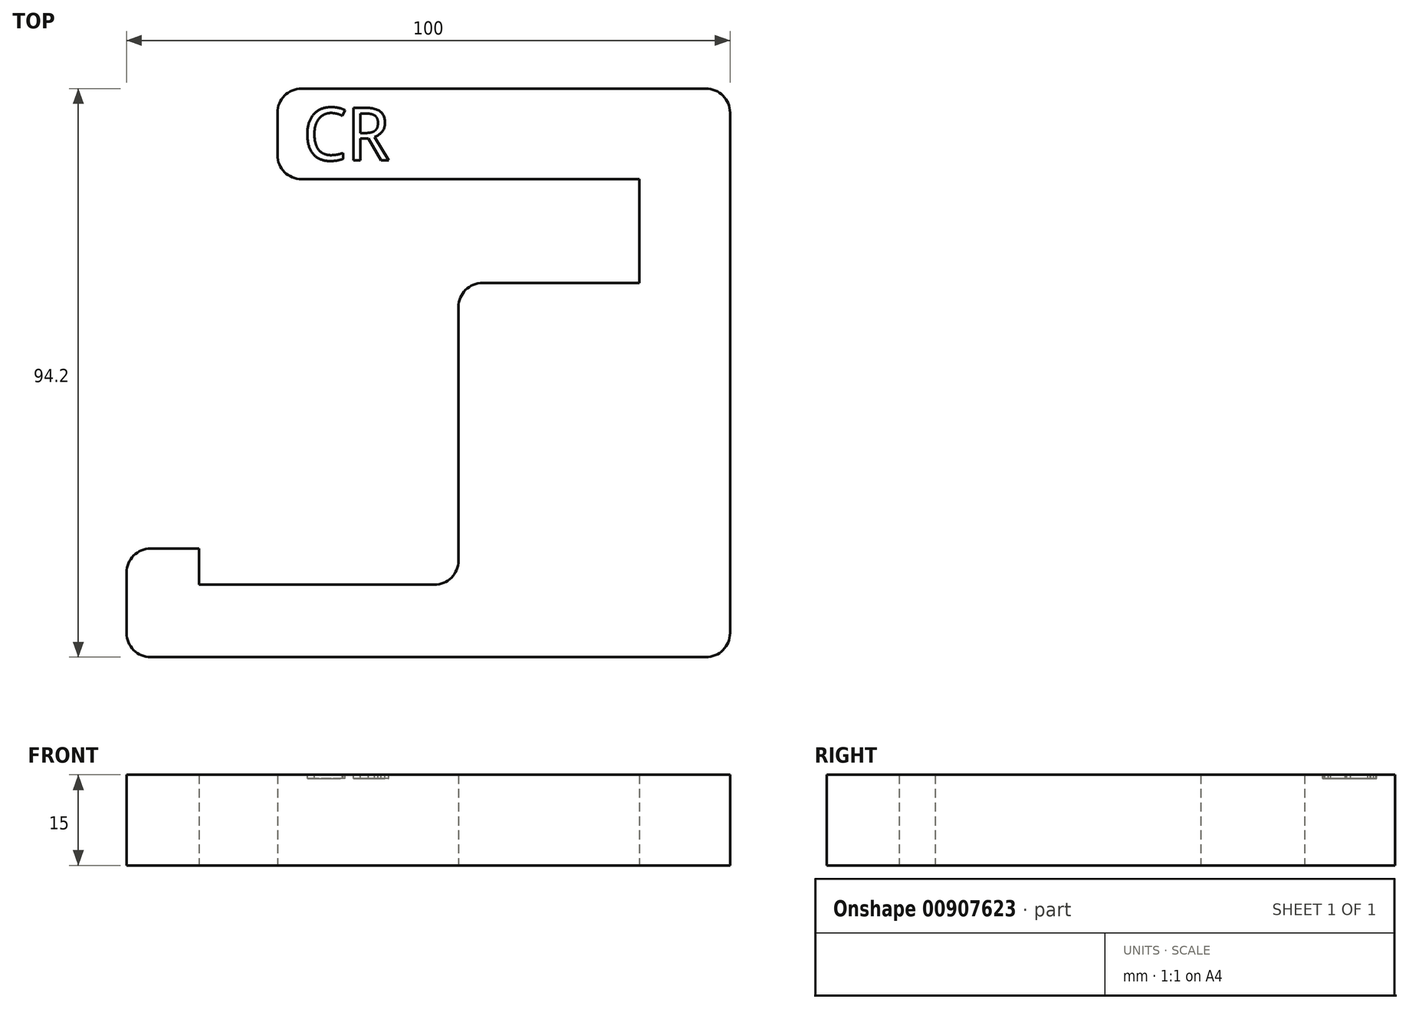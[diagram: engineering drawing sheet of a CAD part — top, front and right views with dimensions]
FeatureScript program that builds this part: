
annotation { "Feature Type Name" : "Feature", "Feature Type Description" : "" }
export const myFeature = defineFeature(function(context is Context, id is Id, definition is map)
    precondition{}
    {
        {
            var Q0;
            Q0=qCreatedBy(makeId("Top.planeOp"),FACE);
            var sketch = newSketch(context, id + "F0", { "sketchPlane" : qUnion([Q0])});
            skLineSegment(sketch, "E0", {"start": v(0, 0) * mm, "end": v(0, -15) * mm});
            skLineSegment(sketch, "E1", {"start": v(0, -15) * mm, "end": v(60, -15) * mm});
            skLineSegment(sketch, "E2", {"start": v(60, -15) * mm, "end": v(60, -32.2) * mm});
            skLineSegment(sketch, "E3", {"start": v(60, -32.2) * mm, "end": v(30, -32.2) * mm});
            skLineSegment(sketch, "E4", {"start": v(30, -32.2) * mm, "end": v(30, -82.2) * mm});
            skLineSegment(sketch, "E5", {"start": v(-25, -94.2) * mm, "end": v(75, -94.2) * mm});
            skLineSegment(sketch, "E6", {"start": v(75, -94.2) * mm, "end": v(75, 0) * mm});
            skLineSegment(sketch, "E7", {"start": v(75, 0) * mm, "end": v(0, 0) * mm});
            skLineSegment(sketch, "E8", {"start": v(-25, -76.2) * mm, "end": v(-13, -76.2) * mm});
            skLineSegment(sketch, "E9", {"start": v(-13, -76.2) * mm, "end": v(-13, -82.2) * mm});
            skLineSegment(sketch, "E10", {"start": v(-13, -82.2) * mm, "end": v(30, -82.2) * mm});
            skLineSegment(sketch, "E11", {"start": v(-25, -76.2) * mm, "end": v(-25, -94.2) * mm});
            skSolve(sketch);
        }
        {
            var Q0;
            Q0=qSketchRegion(id+"F0",true);
            extrude(context, id + "F1", {"entities" : qUnion([Q0]), "depth" : 15 * mm, "offsetDistance" : 25 * mm});
        }
        {
            var Q0;
            Q0=makeQuery(id+"F1.opExtrude","SWEPT_EDGE",EDGE,{"disambiguationData":[OSD([sQuery(id+"F0.wireOp",EDGE,"E3"),sQuery(id+"F0.wireOp",EDGE,"E4")])]});
            var Q1;
            Q1=makeQuery(id+"F1.opExtrude","SWEPT_EDGE",EDGE,{"disambiguationData":[OSD([sQuery(id+"F0.wireOp",EDGE,"E0"),sQuery(id+"F0.wireOp",EDGE,"E1")])]});
            var Q2;
            Q2=makeQuery(id+"F1.opExtrude","SWEPT_EDGE",EDGE,{"disambiguationData":[OSD([sQuery(id+"F0.wireOp",EDGE,"E6"),sQuery(id+"F0.wireOp",EDGE,"E7")])]});
            var Q3;
            Q3=makeQuery(id+"F1.opExtrude","SWEPT_EDGE",EDGE,{"disambiguationData":[OSD([sQuery(id+"F0.wireOp",EDGE,"E5"),sQuery(id+"F0.wireOp",EDGE,"E6")])]});
            var Q4;
            Q4=makeQuery(id+"F1.opExtrude","SWEPT_EDGE",EDGE,{"disambiguationData":[OSD([sQuery(id+"F0.wireOp",EDGE,"E0"),sQuery(id+"F0.wireOp",EDGE,"E7")])]});
            var Q5;
            Q5=makeQuery(id+"F1.opExtrude","SWEPT_EDGE",EDGE,{"disambiguationData":[OSD([sQuery(id+"F0.wireOp",EDGE,"E4"),sQuery(id+"F0.wireOp",EDGE,"BmvVSOrI-arv2-eCNl-y9e8-13uhO79Pgq0i")])]});
            var Q6;
            Q6=makeQuery(id+"F1.opExtrude","SWEPT_EDGE",EDGE,{"disambiguationData":[OSD([sQuery(id+"F0.wireOp",EDGE,"BmvVSOrI-arv2-eCNl-y9e8-13uhO79Pgq0i"),sQuery(id+"F0.wireOp",EDGE,"Or619OzT-ieYu-aD12-7ilh-PgshZOE2rYor")])]});
            var Q7;
            Q7=makeQuery(id+"F1.opExtrude","SWEPT_EDGE",EDGE,{"disambiguationData":[OSD([sQuery(id+"F0.wireOp",EDGE,"Or619OzT-ieYu-aD12-7ilh-PgshZOE2rYor"),sQuery(id+"F0.wireOp",EDGE,"E5")])]});
            var Q8;
            Q8=makeQuery(id+"F1.opExtrude","SWEPT_EDGE",EDGE,{"disambiguationData":[OSD([sQuery(id+"F0.wireOp",EDGE,"E8"),sQuery(id+"F0.wireOp",EDGE,"E11")])]});
            fillet(context, id + "F2", {"entities" : qUnion([Q0, Q1, Q2, Q3, Q4, Q5, Q6, Q7, Q8]), "radius" : 4 * mm, "tangentPropagation" : true, "allowEdgeOverflow" : false});
        }
        {
            var Q0;
            Q0=makeQuery(id+"F1.opExtrude","CAP_FACE",FACE,{"disambiguationData":[OSD([sQuery(id+"F0.wireOp",EDGE,"E0"),sQuery(id+"F0.wireOp",EDGE,"E1"),sQuery(id+"F0.wireOp",EDGE,"E2"),sQuery(id+"F0.wireOp",EDGE,"E3"),sQuery(id+"F0.wireOp",EDGE,"E4"),sQuery(id+"F0.wireOp",EDGE,"E5"),sQuery(id+"F0.wireOp",EDGE,"E6"),sQuery(id+"F0.wireOp",EDGE,"E7"),sQuery(id+"F0.wireOp",EDGE,"E8"),sQuery(id+"F0.wireOp",EDGE,"E9"),sQuery(id+"F0.wireOp",EDGE,"E10"),sQuery(id+"F0.wireOp",EDGE,"E11")])],"isStart":false});
            var sketch = newSketch(context, id + "F3", { "sketchPlane" : qUnion([Q0])});
            skText(sketch, "E12", { "text": "CR", "fontName": "DroidSansMono.ttf"});
            const initialGuessF3  = {"E12": [0.00418, -0.01188, 1, 0, 0.00877]};
            skSetInitialGuess(sketch, initialGuessF3);
            skSolve(sketch);
        }
        {
            var Q0;
            Q0 = qSketchRegion(id + "F3", true);
            extrude(context, id + "F4", {"entities" : qUnion([Q0]), "operationType" : NewBodyOperationType.REMOVE, "oppositeDirection" : true, "depth" : 0.6 * mm, "offsetDistance" : 25 * mm});
        }
    });
